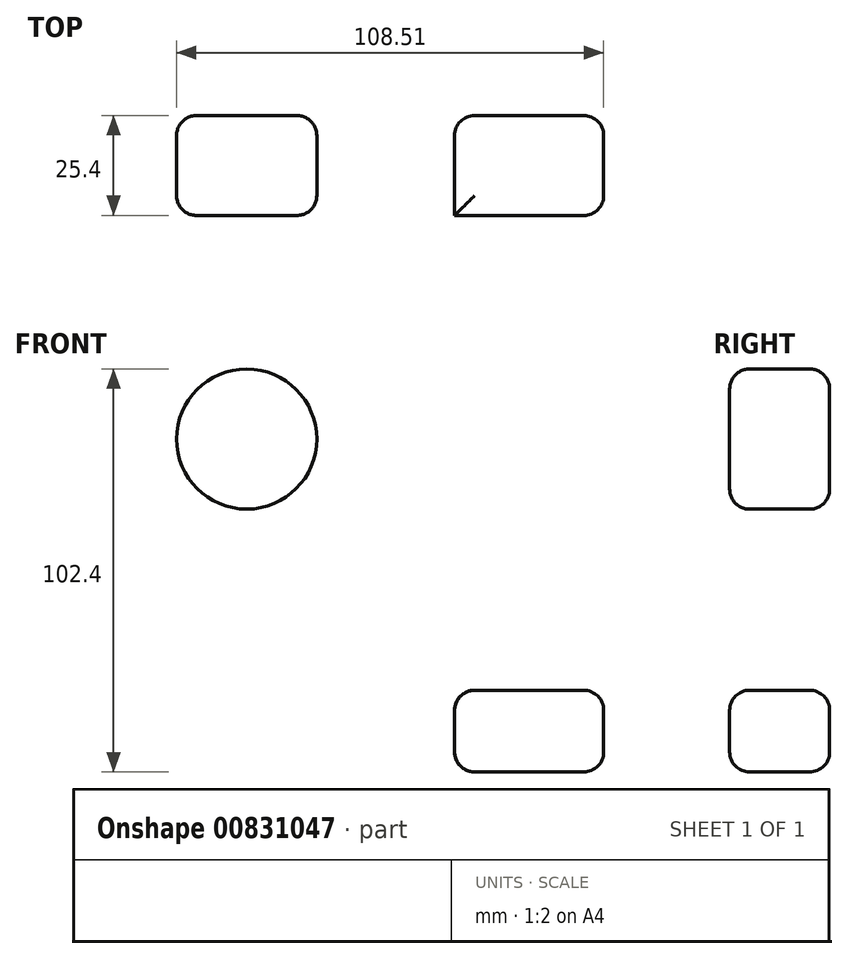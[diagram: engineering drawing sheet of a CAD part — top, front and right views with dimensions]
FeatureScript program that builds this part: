
annotation { "Feature Type Name" : "Feature", "Feature Type Description" : "" }
export const myFeature = defineFeature(function(context is Context, id is Id, definition is map)
    precondition{}
    {
        {
            var Q0;
            Q0=qCreatedBy(makeId("Front.planeOp"),FACE);
            var sketch = newSketch(context, id + "F0", { "sketchPlane" : qUnion([Q0])});
            skCircle(sketch, "E0", {"center": v(-38.63, 31.3) * mm, "radius": 17.8 * mm});
            skLineSegment(sketch, "E1.bottom", {"start": v(14.2, -32.52) * mm, "end": v(52.07, -32.52) * mm});
            skLineSegment(sketch, "E1.top", {"start": v(14.2, -53.29) * mm, "end": v(52.07, -53.29) * mm});
            skLineSegment(sketch, "E1.left", {"start": v(14.2, -32.52) * mm, "end": v(14.2, -53.29) * mm});
            skLineSegment(sketch, "E1.right", {"start": v(52.07, -32.52) * mm, "end": v(52.07, -53.29) * mm});
            skSolve(sketch);
        }
        {
            var Q0;
            Q0=makeQuery(id+"F0.imprint","IMPRINT",FACE,{"disambiguationData":[TD([[makeQuery(id+"F0.imprint","IMPRINT",EDGE,{"derivedFrom":sQuery(id+"F0.wireOp",EDGE,"E0")}),1.0]])]});
            var Q1;
            Q1=makeQuery(id+"F0.imprint","IMPRINT",FACE,{"disambiguationData":[TD([[makeQuery(id+"F0.imprint","IMPRINT",EDGE,{"derivedFrom":sQuery(id+"F0.wireOp",EDGE,"E1.bottom")}),-1.0]])]});
            extrude(context, id + "F1", {"entities" : qUnion([Q0, Q1]), "depth" : 25.4 * mm, "offsetDistance" : 25.4 * mm});
        }
        {
            var Q0;
            Q0=makeQuery(id+"F1.opExtrude","CAP_FACE",FACE,{"disambiguationData":[OSD([sQuery(id+"F0.wireOp",EDGE,"E0")])],"isStart":true});
            var Q1;
            Q1=makeQuery(id+"F1.opExtrude","CAP_FACE",FACE,{"disambiguationData":[OSD([sQuery(id+"F0.wireOp",EDGE,"E1.bottom"),sQuery(id+"F0.wireOp",EDGE,"E1.top"),sQuery(id+"F0.wireOp",EDGE,"E1.left"),sQuery(id+"F0.wireOp",EDGE,"E1.right")])],"isStart":true});
            var Q2;
            Q2=makeQuery(id+"F1.opExtrude","SWEPT_FACE",FACE,{"disambiguationData":[OSD([sQuery(id+"F0.wireOp",EDGE,"E1.right")])]});
            var Q3;
            Q3=makeQuery(id+"F1.opExtrude","CAP_FACE",FACE,{"disambiguationData":[OSD([sQuery(id+"F0.wireOp",EDGE,"E0")])],"isStart":false});
            fillet(context, id + "F2", {"entities" : qUnion([Q0, Q1, Q2, Q3]), "radius" : 5.08 * mm, "tangentPropagation" : true, "allowEdgeOverflow" : false});
        }
        {
            var Q0;
            Q0=makeQuery(id+"F1.opExtrude","SWEPT_FACE",FACE,{"disambiguationData":[OSD([sQuery(id+"F0.wireOp",EDGE,"E1.top")])]});
            var Q1;
            Q1=makeQuery(id+"F1.opExtrude","SWEPT_EDGE",EDGE,{"disambiguationData":[OSD([sQuery(id+"F0.wireOp",EDGE,"E1.bottom"),sQuery(id+"F0.wireOp",EDGE,"E1.left")])]});
            var Q2;
            Q2=makeQuery(id+"F1.opExtrude","CAP_EDGE",EDGE,{"disambiguationData":[OSD([sQuery(id+"F0.wireOp",EDGE,"E1.bottom")])],"isStart":false});
            fillet(context, id + "F3", {"entities" : qUnion([Q0, Q1, Q2]), "radius" : 5.08 * mm, "tangentPropagation" : true, "allowEdgeOverflow" : false});
        }
    });
